# Revit family: SAD-1800_Shrinkwrap_2
name_source: partatom
category: Generic Models
units: mm (PartAtom-declared; Revit-internal decimal feet)

## family parameters
Always vertical = Yes
Can host rebar = No
Cut with Voids When Loaded = No
Part Type = Normal
Room Calculation Point = No
Round Connector Dimension = Use Diameter
Shared = No
Work Plane-Based = No

## types (1)
- Standard
    Default Elevation = 0 mm  [stored 0 ft]
    Manufacturer = 三進金属工業株式会社
    URL = https://www.sanshinkinzoku.co.jp
    タイプ = 標準タイプ 　SAS型 　ディープ
    作業時サッシ開口高さ400mm制御風速 = 0.5m/s
    作業面 = セラミック一体成形焼成品
    品名 = ヒュームフードSシリーズ
    品番 = SAD-1800
    外寸法　奥行-D = 995 mm  [stored 3.26444 ft]
    外寸法　間口-W = 1800 mm  [stored 5.90551 ft]
    外寸法　高さ-H = 2250 mm
    所用ダクト径（φ） = 250mm
    有効内寸法　奥行-D = 790 mm  [stored 2.59186 ft]
    有効内寸法　間口-W = 1550 mm  [stored 5.0853 ft]
    有効内寸法　高さ-H = 1200 mm
    本体材質 = スチール製（粉体塗装仕上げ）
    本体標準色 = マイルドホワイト
    質量 = 480kg
    風量 = 20m3/min

note: [stored X ft] marks values corroborated as IEEE doubles in the binary element streams (Revit-internal decimal feet)

## geometry (parser evidence)
native form markers: Sweep x3
no freeform markers — native parametric forms only
